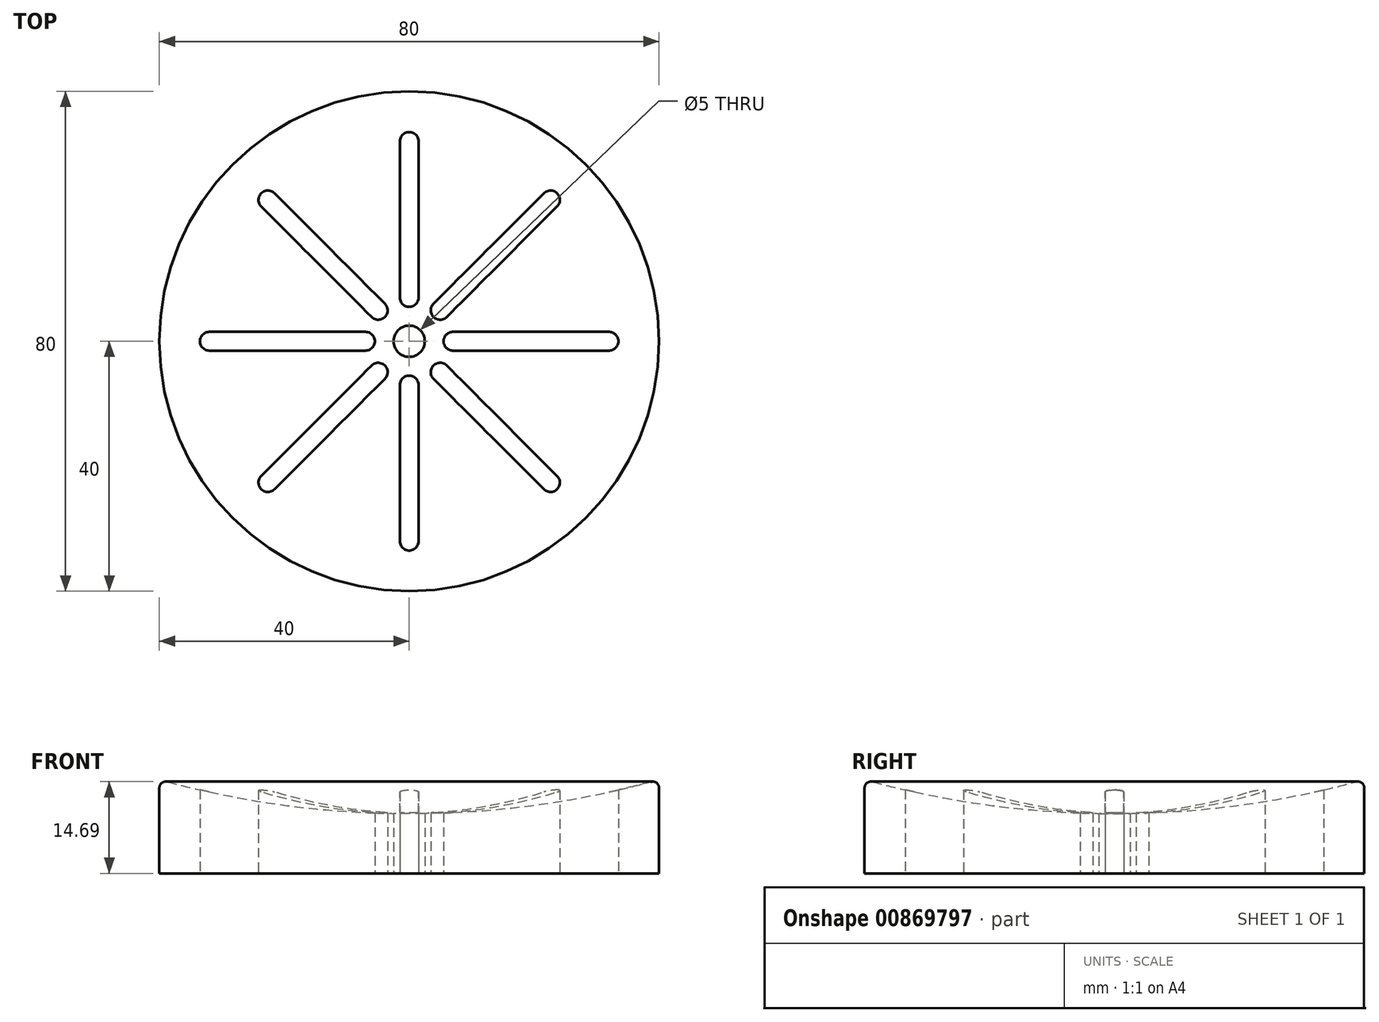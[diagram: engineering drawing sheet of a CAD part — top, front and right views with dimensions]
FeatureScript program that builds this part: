
annotation { "Feature Type Name" : "Feature", "Feature Type Description" : "" }
export const myFeature = defineFeature(function(context is Context, id is Id, definition is map)
    precondition{}
    {
        {
            var Q0;
            Q0=qCreatedBy(makeId("Top.planeOp"),FACE);
            var sketch = newSketch(context, id + "F0", { "sketchPlane" : qUnion([Q0])});
            skCircle(sketch, "E0", {"center": v(0, 0) * mm, "radius": 40 * mm});
            skSolve(sketch);
        }
        {
            var Q0;
            Q0 = qSketchRegion(id + "F0", true);
            extrude(context, id + "F1", {"entities" : qUnion([Q0]), "depth" : 15 * mm, "offsetDistance" : 25 * mm});
        }
        {
            var Q0;
            Q0=qCreatedBy(makeId("Front.planeOp"),FACE);
            var sketch = newSketch(context, id + "F2", { "sketchPlane" : qUnion([Q0])});
            skArc(sketch, "E1", {"start": v(0, 9.57) * mm, "mid": v(20.18, 10.93) * mm, "end": v(40, 15) * mm});
            skLineSegment(sketch, "E2.0.0", {"start": v(0, 15) * mm, "end": v(40, 15) * mm});
            skLineSegment(sketch, "E3", {"start": v(0, 15) * mm, "end": v(0, 9.57) * mm});
            skPoint(sketch, "E4.orphan", {"position": v(-40, 15) * mm});
            skSolve(sketch);
        }
        {
            var Q0;
            Q0 = qSketchRegion(id + "F2", true);
            var Q1;
            Q1=sQuery(id+"F2.wireOp",EDGE,"E3");
            revolve(context, id + "F3", {"operationType" : NewBodyOperationType.REMOVE, "surfaceOperationType" : NewSurfaceOperationType.NEW, "entities" : qUnion([Q0]), "axis" : qUnion([Q1]), "revolveType" : RevolveType.FULL, "oppositeDirection" : true});
        }
        {
            var Q0;
            Q0=makeQuery(id+"F3.boolean.opBoolean","MERGE",EDGE,{"derivedFrom":[makeQuery(id+"F1.opExtrude","CAP_EDGE",EDGE,{"disambiguationData":[OSD([sQuery(id+"F0.wireOp",EDGE,"E0")])],"isStart":false}),makeQuery(id+"F3.opRevolve","SWEPT_EDGE",EDGE,{"disambiguationData":[OSD([sQuery(id+"F2.wireOp",EDGE,"E1"),sQuery(id+"F2.wireOp",EDGE,"E2.0.0")])]})]});
            fillet(context, id + "F4", {"entities" : qUnion([Q0]), "radius" : 1 * mm, "tangentPropagation" : true, "allowEdgeOverflow" : false});
        }
        {
            var Q0;
            Q0=qCreatedBy(makeId("Top.planeOp"),FACE);
            var sketch = newSketch(context, id + "F5", { "sketchPlane" : qUnion([Q0])});
            skCircle(sketch, "E5", {"center": v(0, 0) * mm, "radius": 2.5 * mm});
            skArc(sketch, "E6", {"start": v(1.5, 32) * mm, "mid": v(0, 33.5) * mm, "end": v(-1.5, 32) * mm});
            skArc(sketch, "E7", {"start": v(-1.5, 7) * mm, "mid": v(0, 5.5) * mm, "end": v(1.5, 7) * mm});
            skLineSegment(sketch, "E8", {"start": v(-1.5, 32) * mm, "end": v(-1.5, 7) * mm});
            skLineSegment(sketch, "E9", {"start": v(1.5, 32) * mm, "end": v(1.5, 7) * mm});
            skArc(sketch, "E10.1.0", {"start": v(-21.57, 23.69) * mm, "mid": v(-23.69, 23.69) * mm, "end": v(-23.69, 21.57) * mm});
            skLineSegment(sketch, "E10.1.1", {"start": v(-21.57, 23.69) * mm, "end": v(-3.89, 6.01) * mm});
            skLineSegment(sketch, "E10.1.2", {"start": v(-23.69, 21.57) * mm, "end": v(-6.01, 3.89) * mm});
            skArc(sketch, "E10.1.3", {"start": v(-6.01, 3.89) * mm, "mid": v(-3.89, 3.89) * mm, "end": v(-3.89, 6.01) * mm});
            skArc(sketch, "E10.2.0", {"start": v(-32, 1.5) * mm, "mid": v(-33.5, 0) * mm, "end": v(-32, -1.5) * mm});
            skLineSegment(sketch, "E10.2.1", {"start": v(-32, 1.5) * mm, "end": v(-7, 1.5) * mm});
            skLineSegment(sketch, "E10.2.2", {"start": v(-32, -1.5) * mm, "end": v(-7, -1.5) * mm});
            skArc(sketch, "E10.2.3", {"start": v(-7, -1.5) * mm, "mid": v(-5.5, 0) * mm, "end": v(-7, 1.5) * mm});
            skArc(sketch, "E10.3.0", {"start": v(-23.69, -21.57) * mm, "mid": v(-23.69, -23.69) * mm, "end": v(-21.57, -23.69) * mm});
            skLineSegment(sketch, "E10.3.1", {"start": v(-23.69, -21.57) * mm, "end": v(-6.01, -3.89) * mm});
            skLineSegment(sketch, "E10.3.2", {"start": v(-21.57, -23.69) * mm, "end": v(-3.89, -6.01) * mm});
            skArc(sketch, "E10.3.3", {"start": v(-3.89, -6.01) * mm, "mid": v(-3.89, -3.89) * mm, "end": v(-6.01, -3.89) * mm});
            skArc(sketch, "E10.4.0", {"start": v(-1.5, -32) * mm, "mid": v(0, -33.5) * mm, "end": v(1.5, -32) * mm});
            skLineSegment(sketch, "E10.4.1", {"start": v(-1.5, -32) * mm, "end": v(-1.5, -7) * mm});
            skLineSegment(sketch, "E10.4.2", {"start": v(1.5, -32) * mm, "end": v(1.5, -7) * mm});
            skArc(sketch, "E10.4.3", {"start": v(1.5, -7) * mm, "mid": v(0, -5.5) * mm, "end": v(-1.5, -7) * mm});
            skArc(sketch, "E10.5.0", {"start": v(21.57, -23.69) * mm, "mid": v(23.69, -23.69) * mm, "end": v(23.69, -21.57) * mm});
            skLineSegment(sketch, "E10.5.1", {"start": v(21.57, -23.69) * mm, "end": v(3.89, -6.01) * mm});
            skLineSegment(sketch, "E10.5.2", {"start": v(23.69, -21.57) * mm, "end": v(6.01, -3.89) * mm});
            skArc(sketch, "E10.5.3", {"start": v(6.01, -3.89) * mm, "mid": v(3.89, -3.89) * mm, "end": v(3.89, -6.01) * mm});
            skArc(sketch, "E10.6.0", {"start": v(32, -1.5) * mm, "mid": v(33.5, 0) * mm, "end": v(32, 1.5) * mm});
            skLineSegment(sketch, "E10.6.1", {"start": v(32, -1.5) * mm, "end": v(7, -1.5) * mm});
            skLineSegment(sketch, "E10.6.2", {"start": v(32, 1.5) * mm, "end": v(7, 1.5) * mm});
            skArc(sketch, "E10.6.3", {"start": v(7, 1.5) * mm, "mid": v(5.5, 0) * mm, "end": v(7, -1.5) * mm});
            skArc(sketch, "E10.7.0", {"start": v(23.69, 21.57) * mm, "mid": v(23.69, 23.69) * mm, "end": v(21.57, 23.69) * mm});
            skLineSegment(sketch, "E10.7.1", {"start": v(23.69, 21.57) * mm, "end": v(6.01, 3.89) * mm});
            skLineSegment(sketch, "E10.7.2", {"start": v(21.57, 23.69) * mm, "end": v(3.89, 6.01) * mm});
            skArc(sketch, "E10.7.3", {"start": v(3.89, 6.01) * mm, "mid": v(3.89, 3.89) * mm, "end": v(6.01, 3.89) * mm});
            skLineSegment(sketch, "E10.anchor1", {"start": v(0, 0) * mm, "end": v(-1.5, 32) * mm, "construction": true});
            skLineSegment(sketch, "E10.anchor2", {"start": v(0, 0) * mm, "end": v(21.57, 23.69) * mm, "construction": true});
            skSolve(sketch);
        }
        {
            var Q0;
            Q0 = qSketchRegion(id + "F5", true);
            extrude(context, id + "F6", {"entities" : qUnion([Q0]), "operationType" : NewBodyOperationType.REMOVE, "depth" : 19.6 * mm, "offsetDistance" : 25 * mm});
        }
    });
